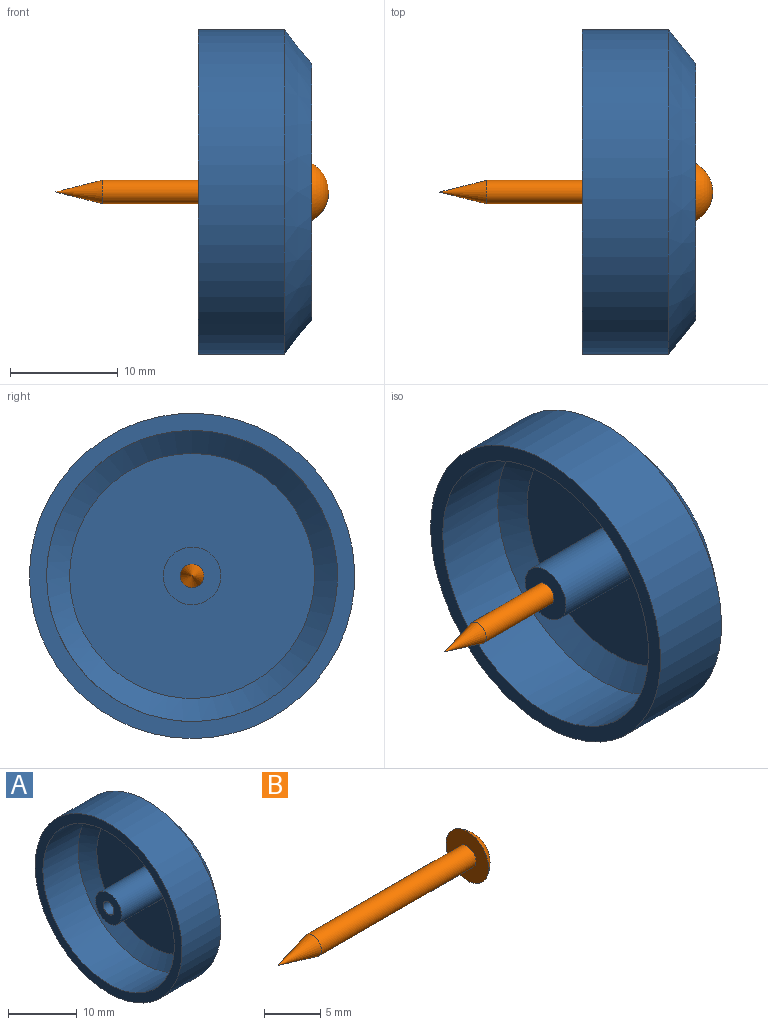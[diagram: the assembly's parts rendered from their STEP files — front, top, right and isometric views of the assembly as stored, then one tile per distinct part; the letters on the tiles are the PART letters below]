
ASSEMBLY  parts=2 mates=1
PART A: 10 faces, bbox 10.5x30.2x30.2 mm
  f0: plane 5.36x5.36mm, normal (-1,0,0), area 18.8mm2, adj f2,f7
  f1: cylinder r=15.11mm len=30.23mm, axis (-1,0,0), area 759.8mm2, adj f4,f5
  f2: cylinder r=1.09mm len=10.54mm, axis (-1,0,0), area 72.3mm2, adj f0,f3
  f3: plane 23.88x23.88mm, normal (1,0,0), area 444mm2, adj f2,f5
  f4: plane 30.23x30.23mm, normal (-1,0,0), area 142.8mm2, adj f1,f6
  f5: cone r=11.94mm half-angle=51.3deg, axis (-1,0,0), area 345.5mm2, adj f1,f3
  f6: cylinder r=13.53mm len=27.05mm, axis (-1,0,0), area 615.1mm2, adj f4,f9
  f7: cylinder r=2.68mm len=8.95mm, axis (-1,0,0), area 150.7mm2, adj f0,f8
  f8: plane 22.76x22.76mm, normal (-1,0,0), area 384.4mm2, adj f7,f9
  f9: cone r=10.95mm half-angle=51.3deg, axis (-1,0,0), area 214.9mm2, adj f6,f8
PART B: 4 faces, bbox 25.4x5.4x5.4 mm
  f0: cylinder r=1.09mm len=19.45mm, axis (1,0,0), area 133.4mm2, adj f1,f3
  f1: cone r=0mm half-angle=14deg, axis (1,0,0), area 15.4mm2, adj f0
  f2: sphere r=3.05mm, area 30.5mm2, adj f3
  f3: plane 5.36x5.36mm, normal (-1,0,0), area 18.8mm2, adj f0,f2
PLACE A t=(0.79,0,0)mm fixed
PLACE B t=(0.79,15.88,0)mm
MATE fastened A.f1 <-> B.f0  axis (1,0,0) through (33.56,15.88,3.18)mm
